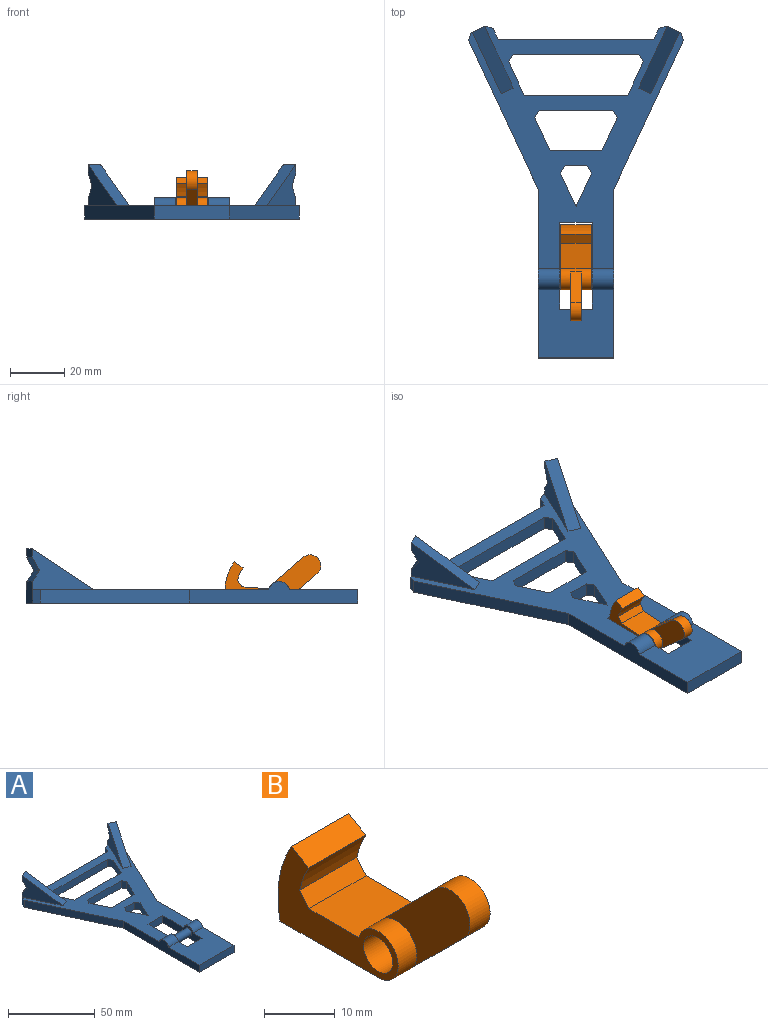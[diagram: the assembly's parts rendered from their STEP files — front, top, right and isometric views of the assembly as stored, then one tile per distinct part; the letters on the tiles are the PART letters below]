
ASSEMBLY  parts=2 mates=1
PART A: 53 faces, bbox 79.2x122.4x20 mm
  f0: plane 28x25.21mm, normal (0,0,1), area 619.4mm2, adj f17,f18,f19,f20,f26,f41,f42,f47
  f1: plane 22.66x15mm, normal (0.91,-0.42,0), area 174mm2, adj f2,f4,f22,f23,f24,f25
  f2: plane 4.53x3mm, normal (0.42,0.91,0), area 15mm2, adj f1,f3,f23,f24
  f3: plane 22.66x15mm, normal (-0.91,0.42,0), area 174mm2, adj f2,f4,f22,f23,f24,f25
  f4: plane 8x5.44mm, normal (0.42,0.91,0), area 45mm2, adj f1,f3,f5,f22,f25,f28,f29
  f5: plane 122.39x79.22mm, normal (0,0,-1), area 3244.5mm2, adj f4,f6,f7,f8,f9,f10,f11,f12
  f6: plane 5x4.01mm, normal (-0.91,0.42,0), area 22.1mm2, adj f5,f7,f22,f28
  f7: plane 57.36x5mm, normal (0,1,0), area 286.8mm2, adj f5,f6,f22,f37
  f8: plane 46.23x5mm, normal (0,-1,0), area 231.1mm2, adj f5,f22,f30,f50
  f9: plane 12.28x5.73mm, normal (-0.91,0.42,0), area 67.8mm2, adj f5,f10,f22,f30
  f10: plane 38.24x5mm, normal (0,1,0), area 191.2mm2, adj f5,f9,f22,f38
  f11: plane 27.11x5mm, normal (0,-1,0), area 135.5mm2, adj f5,f22,f32,f52
  f12: plane 12.28x5.73mm, normal (-0.91,0.42,0), area 67.8mm2, adj f5,f13,f22,f32
  f13: plane 19.12x5mm, normal (0,1,0), area 95.6mm2, adj f5,f12,f22,f39
  f14: plane 7.99x5mm, normal (0,-1,0), area 39.9mm2, adj f5,f22,f31,f51
  f15: plane 12.28x5.73mm, normal (-0.91,0.42,0), area 67.8mm2, adj f5,f22,f31,f40
  f16: plane 12x5mm, normal (0,-1,0), area 60mm2, adj f5,f17,f22,f41
  f17: plane 32x8mm, normal (-1,0,0), area 157.6mm2, adj f0,f5,f16,f18,f22,f26,f27
  f18: plane 12x5mm, normal (0,1,0), area 60mm2, adj f0,f5,f17,f41
  f19: plane 28x5mm, normal (0,-1,0), area 140mm2, adj f0,f5,f20,f42
  f20: plane 62.28x8mm, normal (1,0,0), area 328.6mm2, adj f0,f5,f19,f21,f22,f26
  f21: plane 54.92x25.61mm, normal (0.91,-0.42,0), area 303mm2, adj f5,f20,f22,f29
  f22: plane 89.43x79.22mm, normal (0,0,1), area 2251.2mm2, adj f1,f3,f4,f6,f7,f8,f9,f10
  f23: plane 24.77x15.1mm, normal (-0.22,-0.47,0.86), area 145.8mm2, adj f1,f2,f3,f22
  f24: plane 5.8x5mm, normal (0.36,0.78,-0.51), area 29.2mm2, adj f1,f2,f3,f25
  f25: plane 5.8x4.83mm, normal (0.34,0.73,0.6), area 25mm2, adj f1,f3,f4,f24
  f26: cylinder r=4mm len=8mm, axis (1,0,0), area 84.4mm2, adj f0,f17,f20,f22
  f27: cylinder r=2.5mm len=12mm, axis (1,0,0), area 188.5mm2, adj f17,f41
  f28: plane 5x2.66mm, normal (-0.34,0.94,0), area 14.1mm2, adj f4,f5,f6,f22
  f29: plane 5x2.66mm, normal (0.94,0.34,0), area 14.1mm2, adj f4,f5,f21,f22
  f30: plane 5x2.72mm, normal (-0.84,-0.54,0), area 16.1mm2, adj f5,f8,f9,f22
  f31: plane 5x2.72mm, normal (-0.84,-0.54,0), area 16.1mm2, adj f5,f14,f15,f22
  f32: plane 5x2.72mm, normal (-0.84,-0.54,0), area 16.1mm2, adj f5,f11,f12,f22
  f33: plane 22.66x15mm, normal (-0.91,-0.42,0), area 174mm2, adj f22,f34,f36,f44,f45,f46
  f34: plane 4.53x3mm, normal (-0.42,0.91,0), area 15mm2, adj f33,f35,f44,f45
  f35: plane 22.66x15mm, normal (0.91,0.42,0), area 174mm2, adj f22,f34,f36,f44,f45,f46
  f36: plane 8x5.44mm, normal (-0.42,0.91,0), area 45mm2, adj f5,f22,f33,f35,f46,f48,f49
  f37: plane 5x4.01mm, normal (0.91,0.42,0), area 22.1mm2, adj f5,f7,f22,f48
  f38: plane 12.28x5.73mm, normal (0.91,0.42,0), area 67.8mm2, adj f5,f10,f22,f50
  f39: plane 12.28x5.73mm, normal (0.91,0.42,0), area 67.8mm2, adj f5,f13,f22,f52
  f40: plane 12.28x5.73mm, normal (0.91,0.42,0), area 67.8mm2, adj f5,f15,f22,f51
  f41: plane 32x8mm, normal (1,0,0), area 157.6mm2, adj f0,f5,f16,f18,f22,f27,f47
  f42: plane 62.28x8mm, normal (-1,0,0), area 328.6mm2, adj f0,f5,f19,f22,f43,f47
  f43: plane 54.92x25.61mm, normal (-0.91,-0.42,0), area 303mm2, adj f5,f22,f42,f49
  f44: plane 24.77x15.1mm, normal (0.22,-0.47,0.86), area 145.8mm2, adj f22,f33,f34,f35
  f45: plane 5.8x5mm, normal (-0.36,0.78,-0.51), area 29.2mm2, adj f33,f34,f35,f46
  f46: plane 5.8x4.83mm, normal (-0.34,0.73,0.6), area 25mm2, adj f33,f35,f36,f45
  f47: cylinder r=4mm len=8mm, axis (-1,0,0), area 84.4mm2, adj f0,f22,f41,f42
  f48: plane 5x2.66mm, normal (0.34,0.94,0), area 14.1mm2, adj f5,f22,f36,f37
  f49: plane 5x2.66mm, normal (-0.94,0.34,0), area 14.1mm2, adj f5,f22,f36,f43
  f50: plane 5x2.72mm, normal (0.84,-0.54,0), area 16.1mm2, adj f5,f8,f22,f38
  f51: plane 5x2.72mm, normal (0.84,-0.54,0), area 16.1mm2, adj f5,f14,f22,f40
  f52: plane 5x2.72mm, normal (0.84,-0.54,0), area 16.1mm2, adj f5,f11,f22,f39
PART B: 15 faces, bbox 11.4x34.6x18.6 mm
  f0: cylinder r=4mm len=11.4mm, axis (-1,0,0), area 153.1mm2, adj f1,f5,f6,f8,f10,f11,f13,f14
  f1: plane 19.6x11.4mm, normal (0,0,-1), area 223.4mm2, adj f0,f2,f6,f13
  f2: cylinder r=20mm len=14mm, axis (-1,0,0), area 165.3mm2, adj f1,f3,f6,f13
  f3: plane 11.4x3.46mm, normal (0,-0.5,0.87), area 45.6mm2, adj f2,f4,f6,f13
  f4: cylinder r=16mm len=11.4mm, axis (-1,0,0), area 58.1mm2, adj f3,f6,f12,f13
  f5: plane 11.4x9.95mm, normal (0,0,1), area 113.5mm2, adj f0,f6,f12,f13
  f6: plane 24x14mm, normal (1,0,0), area 143mm2, adj f0,f1,f2,f3,f4,f5,f7,f12
  f7: cylinder r=2.9mm len=11.4mm, axis (1,0,0), area 207.7mm2, adj f6,f13
  f8: plane 10.61x10.61mm, normal (0,0.71,0.71), area 60mm2, adj f0,f9,f11,f14
  f9: cylinder r=4mm len=6.83mm, axis (-1,0,0), area 50.3mm2, adj f8,f10,f11,f14
  f10: plane 10.61x10.61mm, normal (0,-0.71,-0.71), area 60mm2, adj f0,f9,f11,f14
  f11: plane 17.44x17.44mm, normal (1,0,0), area 120mm2, adj f0,f8,f9,f10
  f12: plane 11.4x2.26mm, normal (0,-0.78,0.63), area 33.2mm2, adj f4,f5,f6,f13
  f13: plane 24x14mm, normal (-1,0,0), area 143mm2, adj f0,f1,f2,f3,f4,f5,f7,f12
  f14: plane 17.44x17.44mm, normal (-1,0,0), area 120mm2, adj f0,f8,f9,f10
PLACE A t=(0,32.74,-5)mm
PLACE B rot(axis=(1,0,0),4.3deg) t=(0,32.99,-3.88)mm
MATE revolute B.f7 <-> A.f27  axis (1,0,0) through (2,17.74,-1)mm
